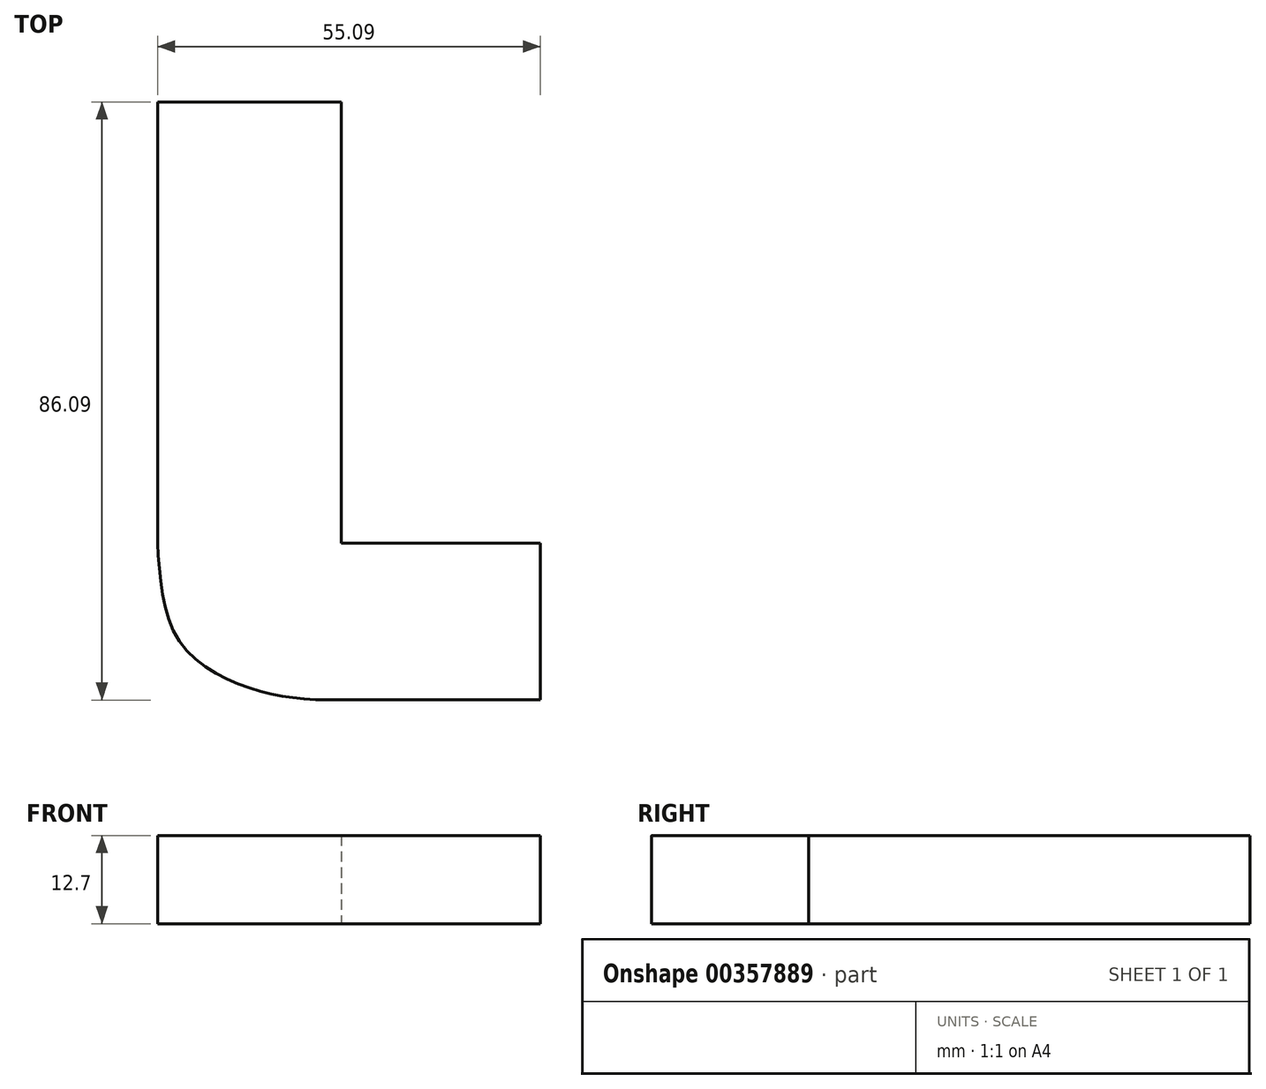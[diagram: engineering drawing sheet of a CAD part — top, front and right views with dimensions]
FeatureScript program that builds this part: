
annotation { "Feature Type Name" : "Feature", "Feature Type Description" : "" }
export const myFeature = defineFeature(function(context is Context, id is Id, definition is map)
    precondition{}
    {
        {
            var Q0;
            Q0=qCreatedBy(makeId("Top.planeOp"),FACE);
            var sketch = newSketch(context, id + "F0", { "sketchPlane" : qUnion([Q0])});
            skLineSegment(sketch, "E0.bottom", {"start": v(0, 0) * mm, "end": v(-26.47, 0) * mm});
            skLineSegment(sketch, "E0.top", {"start": v(0, 63.5) * mm, "end": v(-26.47, 63.5) * mm});
            skLineSegment(sketch, "E0.left", {"start": v(0, 0) * mm, "end": v(0, 63.5) * mm});
            skLineSegment(sketch, "E0.right", {"start": v(-26.47, 0) * mm, "end": v(-26.47, 63.5) * mm});
            skLineSegment(sketch, "E1.bottom", {"start": v(0, 0) * mm, "end": v(28.62, 0) * mm});
            skLineSegment(sketch, "E1.top", {"start": v(0, -22.58) * mm, "end": v(28.62, -22.58) * mm});
            skLineSegment(sketch, "E1.left", {"start": v(0, 0) * mm, "end": v(0, -22.58) * mm});
            skLineSegment(sketch, "E1.right", {"start": v(28.62, 0) * mm, "end": v(28.62, -22.58) * mm});
            skFitSpline(sketch, "E2", {"points": [v(-26.47, 0) * mm, v(-23.33, -14.14) * mm, v(-12.26, -21.16) * mm, v(0, -22.58) * mm], "startDerivative": vector(2.62, -39.97) * mm, "endDerivative": vector(45.82, 0.38) * mm});
            skSolve(sketch);
        }
        {
            var Q0;
            Q0 = qSketchRegion(id + "F0", true);
            extrude(context, id + "F1", {"entities" : qUnion([Q0]), "depth" : 12.7 * mm});
        }
    });
